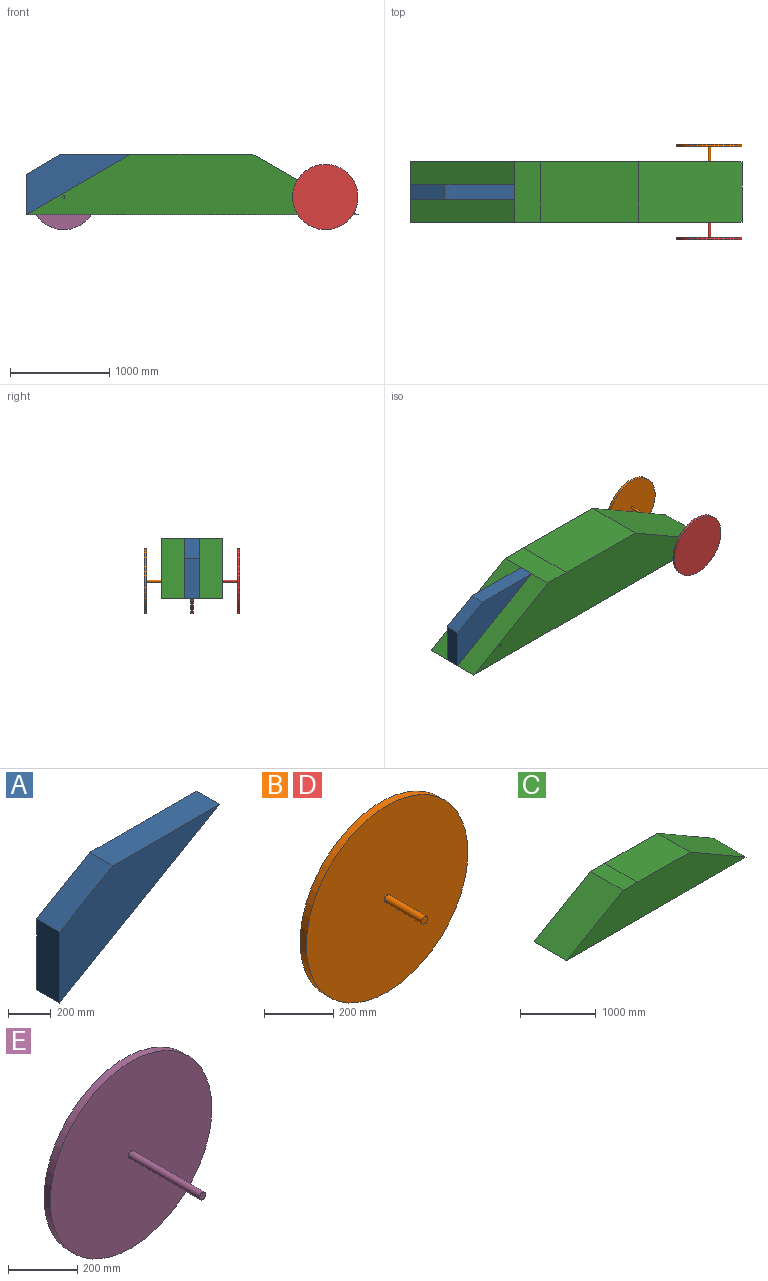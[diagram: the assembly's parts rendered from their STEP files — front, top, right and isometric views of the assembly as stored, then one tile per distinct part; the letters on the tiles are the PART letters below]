
ASSEMBLY  parts=5 mates=4
PART A: 6 faces, bbox 1056.9x152.4x610.2 mm
  f0: plane 406.4x152.4mm, normal (-1,0,0), area 61935.4mm2, adj f1,f3,f4,f5
  f1: plane 1056.92x610.21mm, normal (0.5,0,-0.87), area 185993mm2, adj f0,f2,f4,f5
  f2: plane 703.91x152.4mm, normal (0,0,1), area 107275.2mm2, adj f1,f3,f4,f5
  f3: plane 353.01x203.81mm, normal (-0.5,0,0.87), area 62122.2mm2, adj f0,f2,f4,f5
  f4: plane 1056.92x610.21mm, normal (0,-1,0), area 286498.7mm2, adj f0,f1,f2,f3
  f5: plane 1056.92x610.21mm, normal (0,1,0), area 286498.7mm2, adj f0,f1,f2,f3
PART B: 5 faces, bbox 660.4x177.8x660.4 mm
  f0: cylinder r=330.2mm len=660.4mm, axis (0,1,0), area 52697.6mm2, adj f1,f2
  f1: plane 660.4x660.4mm, normal (0,-1,0), area 342027.5mm2, adj f0,f3
  f2: plane 660.4x660.4mm, normal (0,1,0), area 342534.3mm2, adj f0
  f3: cylinder r=12.7mm len=152.4mm, axis (0,1,0), area 12161mm2, adj f1,f4
  f4: plane 25.4x25.4mm, normal (0,-1,0), area 506.7mm2, adj f3
PART C: 7 faces, bbox 3352.8x609.6x610.2 mm
  f0: plane 3352.8x609.6mm, normal (0,0,-1), area 2043866.9mm2, adj f1,f4,f5,f6
  f1: plane 1043.45x609.6mm, normal (0.5,0,0.87), area 734491.1mm2, adj f0,f2,f5,f6
  f2: plane 988.55x609.6mm, normal (0.01,0,1), area 602635mm2, adj f1,f3,f5,f6
  f3: plane 609.6x263.88mm, normal (0,0,1), area 160861.6mm2, adj f2,f4,f5,f6
  f4: plane 1056.92x610.21mm, normal (-0.5,0,0.87), area 743971.8mm2, adj f0,f3,f5,f6
  f5: plane 3352.8x610.21mm, normal (0,-1,0), area 1396800.9mm2, adj f0,f1,f2,f3,f4
  f6: plane 3352.8x610.21mm, normal (0,1,0), area 1396800.9mm2, adj f0,f1,f2,f3,f4
PART D: same geometry as B
PART E: 5 faces, bbox 660.4x317.5x660.4 mm
  f0: cylinder r=12.7mm len=292.1mm, axis (0,1,0), area 23308.5mm2, adj f1,f3
  f1: plane 25.4x25.4mm, normal (0,-1,0), area 506.7mm2, adj f0
  f2: cylinder r=330.2mm len=660.4mm, axis (0,1,0), area 52697.6mm2, adj f3,f4
  f3: plane 660.4x660.4mm, normal (0,-1,0), area 342027.5mm2, adj f0,f2
  f4: plane 660.4x660.4mm, normal (0,1,0), area 342534.3mm2, adj f2
PLACE A t=(-2670.12,-381,228.91)mm
PLACE B t=(0,25.4,0)mm
PLACE C t=(-2999.68,-152.4,-408.2)mm
PLACE D rot(axis=(0,0,-1),180deg) t=(0,-939.8,0)mm
PLACE E t=(-2599.3,-444.5,-32.31)mm
MATE fastened E.f0 <-> C.f5  axis (0,-1,0) through (-2641.6,-762,0)mm
MATE fastened C.f4 <-> A.f1  axis (-0.5,0,0.87) through (-3022.6,-457.2,-177.8)mm
MATE fastened C.f5 <-> D.f3  axis (0,-1,0) through (0,-762,0)mm
MATE fastened C.f6 <-> B.f3  axis (0,1,0) through (0,-152.4,0)mm
